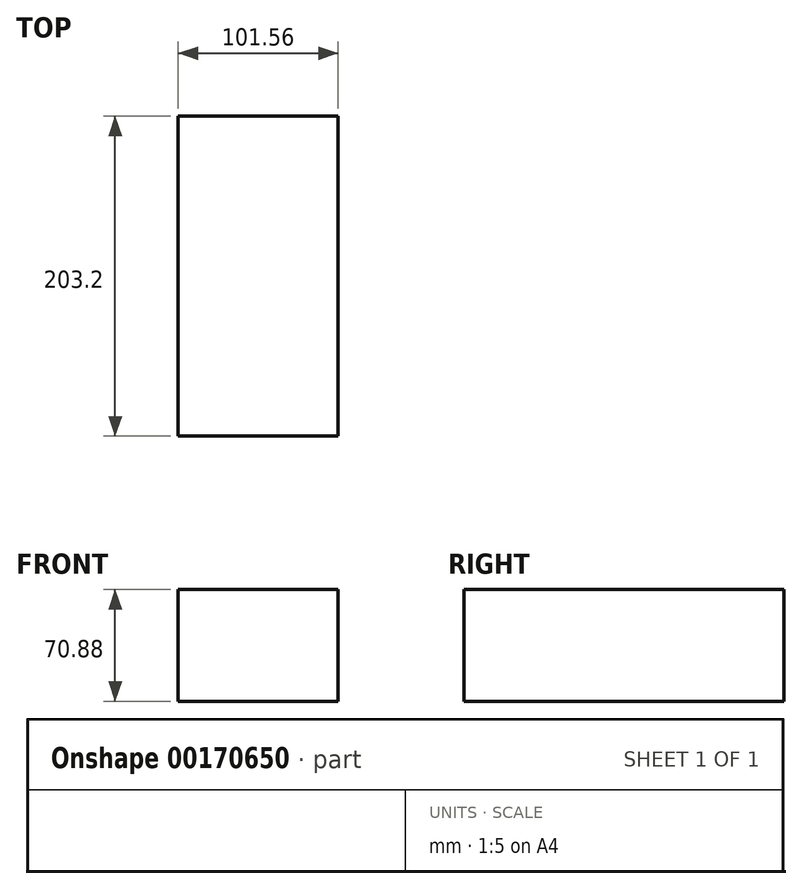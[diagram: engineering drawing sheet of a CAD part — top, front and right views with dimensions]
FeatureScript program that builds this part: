
annotation { "Feature Type Name" : "Feature", "Feature Type Description" : "" }
export const myFeature = defineFeature(function(context is Context, id is Id, definition is map)
    precondition{}
    {
        {
            var Q0;
            Q0=qCreatedBy(makeId("Front.planeOp"),FACE);
            var sketch = newSketch(context, id + "F0", { "sketchPlane" : qUnion([Q0])});
            skLineSegment(sketch, "E0.bottom", {"start": v(0, 54.57) * mm, "end": v(101.56, 54.57) * mm});
            skLineSegment(sketch, "E0.top", {"start": v(0, -16.31) * mm, "end": v(101.56, -16.31) * mm});
            skLineSegment(sketch, "E0.left", {"start": v(0, 54.57) * mm, "end": v(0, -16.31) * mm});
            skLineSegment(sketch, "E0.right", {"start": v(101.56, 54.57) * mm, "end": v(101.56, -16.31) * mm});
            skPoint(sketch, "E0.middle", {"position": v(50.78, 19.13) * mm});
            skSolve(sketch);
        }
        {
            var Q0;
            Q0 = qSketchRegion(id + "F0", true);
            extrude(context, id + "F1", {"entities" : qUnion([Q0]), "depth" : 203.2 * mm});
        }
    });
